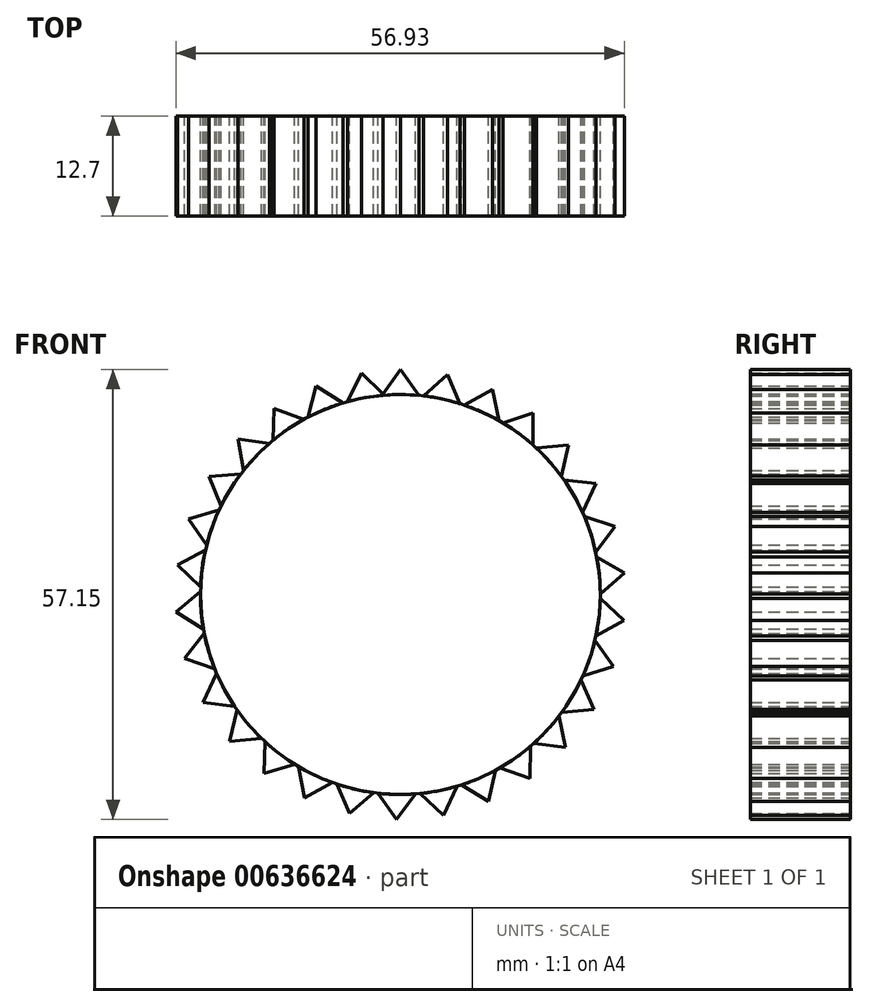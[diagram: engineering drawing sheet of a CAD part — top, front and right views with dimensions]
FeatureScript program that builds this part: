
annotation { "Feature Type Name" : "Feature", "Feature Type Description" : "" }
export const myFeature = defineFeature(function(context is Context, id is Id, definition is map)
    precondition{}
    {
        {
            var Q0;
            Q0=qCreatedBy(makeId("Front.planeOp"),FACE);
            var sketch = newSketch(context, id + "F0", { "sketchPlane" : qUnion([Q0])});
            skCircle(sketch, "E0", {"center": v(0, 0) * mm, "radius": 25.4 * mm});
            skLineSegment(sketch, "E1", {"start": v(0, 25.4) * mm, "end": v(0, 28.58) * mm});
            skLineSegment(sketch, "E2", {"start": v(0, 28.58) * mm, "end": v(-2.37, 25.29) * mm});
            skLineSegment(sketch, "E3.MirrorCS", {"start": v(0, 28.58) * mm, "end": v(2.37, 25.29) * mm});
            skLineSegment(sketch, "E4.1.0", {"start": v(5.97, 27.94) * mm, "end": v(2.97, 25.23) * mm});
            skLineSegment(sketch, "E4.1.1", {"start": v(5.97, 27.94) * mm, "end": v(7.6, 24.23) * mm});
            skLineSegment(sketch, "E4.2.0", {"start": v(11.69, 26.08) * mm, "end": v(8.17, 24.05) * mm});
            skLineSegment(sketch, "E4.2.1", {"start": v(11.69, 26.08) * mm, "end": v(12.5, 22.1) * mm});
            skLineSegment(sketch, "E4.3.0", {"start": v(16.88, 23.06) * mm, "end": v(13.02, 21.8) * mm});
            skLineSegment(sketch, "E4.3.1", {"start": v(16.88, 23.06) * mm, "end": v(16.85, 19) * mm});
            skLineSegment(sketch, "E4.4.0", {"start": v(21.33, 19.02) * mm, "end": v(17.3, 18.6) * mm});
            skLineSegment(sketch, "E4.4.1", {"start": v(21.33, 19.02) * mm, "end": v(20.45, 15.06) * mm});
            skLineSegment(sketch, "E4.5.0", {"start": v(24.83, 14.14) * mm, "end": v(20.8, 14.58) * mm});
            skLineSegment(sketch, "E4.5.1", {"start": v(24.83, 14.14) * mm, "end": v(23.15, 10.45) * mm});
            skLineSegment(sketch, "E4.6.0", {"start": v(27.24, 8.63) * mm, "end": v(23.39, 9.9) * mm});
            skLineSegment(sketch, "E4.6.1", {"start": v(27.24, 8.63) * mm, "end": v(24.82, 5.38) * mm});
            skLineSegment(sketch, "E4.7.0", {"start": v(28.44, 2.75) * mm, "end": v(24.94, 4.8) * mm});
            skLineSegment(sketch, "E4.7.1", {"start": v(28.44, 2.75) * mm, "end": v(25.4, 0.07) * mm});
            skLineSegment(sketch, "E4.8.0", {"start": v(28.39, -3.26) * mm, "end": v(25.4, -0.53) * mm});
            skLineSegment(sketch, "E4.8.1", {"start": v(28.39, -3.26) * mm, "end": v(24.85, -5.24) * mm});
            skLineSegment(sketch, "E4.9.0", {"start": v(27.08, -9.12) * mm, "end": v(24.72, -5.82) * mm});
            skLineSegment(sketch, "E4.9.1", {"start": v(27.08, -9.12) * mm, "end": v(23.2, -10.32) * mm});
            skLineSegment(sketch, "E4.10.0", {"start": v(24.57, -14.58) * mm, "end": v(22.96, -10.87) * mm});
            skLineSegment(sketch, "E4.10.1", {"start": v(24.57, -14.58) * mm, "end": v(20.54, -14.95) * mm});
            skLineSegment(sketch, "E4.11.0", {"start": v(20.98, -19.4) * mm, "end": v(20.18, -15.43) * mm});
            skLineSegment(sketch, "E4.11.1", {"start": v(20.98, -19.4) * mm, "end": v(16.96, -18.91) * mm});
            skLineSegment(sketch, "E4.12.0", {"start": v(16.46, -23.36) * mm, "end": v(16.5, -19.3) * mm});
            skLineSegment(sketch, "E4.12.1", {"start": v(16.46, -23.36) * mm, "end": v(12.63, -22.04) * mm});
            skLineSegment(sketch, "E4.13.0", {"start": v(11.21, -26.28) * mm, "end": v(12.1, -22.33) * mm});
            skLineSegment(sketch, "E4.13.1", {"start": v(11.21, -26.28) * mm, "end": v(7.74, -24.2) * mm});
            skLineSegment(sketch, "E4.14.0", {"start": v(5.47, -28.05) * mm, "end": v(7.17, -24.37) * mm});
            skLineSegment(sketch, "E4.14.1", {"start": v(5.47, -28.05) * mm, "end": v(2.5, -25.28) * mm});
            skLineSegment(sketch, "E4.15.0", {"start": v(-0.52, -28.57) * mm, "end": v(1.92, -25.33) * mm});
            skLineSegment(sketch, "E4.15.1", {"start": v(-0.52, -28.57) * mm, "end": v(-2.83, -25.24) * mm});
            skLineSegment(sketch, "E4.16.0", {"start": v(-6.48, -27.83) * mm, "end": v(-3.42, -25.17) * mm});
            skLineSegment(sketch, "E4.16.1", {"start": v(-6.48, -27.83) * mm, "end": v(-8.05, -24.1) * mm});
            skLineSegment(sketch, "E4.17.0", {"start": v(-12.15, -25.86) * mm, "end": v(-8.6, -23.9) * mm});
            skLineSegment(sketch, "E4.17.1", {"start": v(-12.15, -25.86) * mm, "end": v(-12.9, -21.88) * mm});
            skLineSegment(sketch, "E4.18.0", {"start": v(-17.3, -22.75) * mm, "end": v(-13.41, -21.57) * mm});
            skLineSegment(sketch, "E4.18.1", {"start": v(-17.3, -22.75) * mm, "end": v(-17.2, -18.7) * mm});
            skLineSegment(sketch, "E4.19.0", {"start": v(-21.67, -18.63) * mm, "end": v(-17.63, -18.29) * mm});
            skLineSegment(sketch, "E4.19.1", {"start": v(-21.67, -18.63) * mm, "end": v(-20.72, -14.69) * mm});
            skLineSegment(sketch, "E4.20.0", {"start": v(-25.08, -13.69) * mm, "end": v(-21.06, -14.2) * mm});
            skLineSegment(sketch, "E4.20.1", {"start": v(-25.08, -13.69) * mm, "end": v(-23.34, -10.03) * mm});
            skLineSegment(sketch, "E4.21.0", {"start": v(-27.4, -8.14) * mm, "end": v(-23.56, -9.48) * mm});
            skLineSegment(sketch, "E4.21.1", {"start": v(-27.4, -8.14) * mm, "end": v(-24.92, -4.93) * mm});
            skLineSegment(sketch, "E4.22.0", {"start": v(-28.49, -2.23) * mm, "end": v(-25.03, -4.34) * mm});
            skLineSegment(sketch, "E4.22.1", {"start": v(-28.49, -2.23) * mm, "end": v(-25.4, 0.4) * mm});
            skLineSegment(sketch, "E4.23.0", {"start": v(-28.32, 3.77) * mm, "end": v(-25.38, 0.98) * mm});
            skLineSegment(sketch, "E4.23.1", {"start": v(-28.32, 3.77) * mm, "end": v(-24.75, 5.7) * mm});
            skLineSegment(sketch, "E4.24.0", {"start": v(-26.91, 9.61) * mm, "end": v(-24.61, 6.27) * mm});
            skLineSegment(sketch, "E4.24.1", {"start": v(-26.91, 9.61) * mm, "end": v(-23.02, 10.74) * mm});
            skLineSegment(sketch, "E4.25.0", {"start": v(-24.3, 15.03) * mm, "end": v(-22.76, 11.28) * mm});
            skLineSegment(sketch, "E4.25.1", {"start": v(-24.3, 15.03) * mm, "end": v(-20.26, 15.32) * mm});
            skLineSegment(sketch, "E4.26.0", {"start": v(-20.63, 19.78) * mm, "end": v(-19.9, 15.79) * mm});
            skLineSegment(sketch, "E4.26.1", {"start": v(-20.63, 19.78) * mm, "end": v(-16.61, 19.22) * mm});
            skLineSegment(sketch, "E4.27.0", {"start": v(-16.04, 23.65) * mm, "end": v(-16.16, 19.6) * mm});
            skLineSegment(sketch, "E4.27.1", {"start": v(-16.04, 23.65) * mm, "end": v(-12.23, 22.26) * mm});
            skLineSegment(sketch, "E4.28.0", {"start": v(-10.74, 26.48) * mm, "end": v(-11.7, 22.54) * mm});
            skLineSegment(sketch, "E4.28.1", {"start": v(-10.74, 26.48) * mm, "end": v(-7.3, 24.33) * mm});
            skLineSegment(sketch, "E4.29.0", {"start": v(-4.96, 28.14) * mm, "end": v(-6.73, 24.5) * mm});
            skLineSegment(sketch, "E4.29.1", {"start": v(-4.96, 28.14) * mm, "end": v(-2.05, 25.32) * mm});
            skLineSegment(sketch, "E4.anchor1", {"start": v(0, 0) * mm, "end": v(-2.37, 25.29) * mm, "construction": true});
            skLineSegment(sketch, "E4.anchor2", {"start": v(0, 0) * mm, "end": v(-6.73, 24.5) * mm, "construction": true});
            skSolve(sketch);
        }
        {
            var Q0;
            {var subQ0=sQuery(id+"F0.wireOp",EDGE,"E4.1.0");Q0=makeQuery(id+"F0.imprint","IMPRINT",FACE,{"disambiguationData":[TD([[makeQuery(id+"F0.imprint","IMPRINT",EDGE,{"derivedFrom":subQ0}),1.0]])]});}
            var Q1;
            {var subQ0=sQuery(id+"F0.wireOp",EDGE,"E4.2.0");Q1=makeQuery(id+"F0.imprint","IMPRINT",FACE,{"disambiguationData":[TD([[makeQuery(id+"F0.imprint","IMPRINT",EDGE,{"derivedFrom":subQ0}),1.0]])]});}
            var Q2;
            {var subQ0=sQuery(id+"F0.wireOp",EDGE,"E4.3.0");Q2=makeQuery(id+"F0.imprint","IMPRINT",FACE,{"disambiguationData":[TD([[makeQuery(id+"F0.imprint","IMPRINT",EDGE,{"derivedFrom":subQ0}),1.0]])]});}
            var Q3;
            {var subQ0=sQuery(id+"F0.wireOp",EDGE,"E4.4.0");Q3=makeQuery(id+"F0.imprint","IMPRINT",FACE,{"disambiguationData":[TD([[makeQuery(id+"F0.imprint","IMPRINT",EDGE,{"derivedFrom":subQ0}),1.0]])]});}
            var Q4;
            {var subQ0=sQuery(id+"F0.wireOp",EDGE,"E4.5.0");Q4=makeQuery(id+"F0.imprint","IMPRINT",FACE,{"disambiguationData":[TD([[makeQuery(id+"F0.imprint","IMPRINT",EDGE,{"derivedFrom":subQ0}),1.0]])]});}
            var Q5;
            {var subQ0=sQuery(id+"F0.wireOp",EDGE,"E4.6.0");Q5=makeQuery(id+"F0.imprint","IMPRINT",FACE,{"disambiguationData":[TD([[makeQuery(id+"F0.imprint","IMPRINT",EDGE,{"derivedFrom":subQ0}),1.0]])]});}
            var Q6;
            {var subQ0=sQuery(id+"F0.wireOp",EDGE,"E4.7.0");Q6=makeQuery(id+"F0.imprint","IMPRINT",FACE,{"disambiguationData":[TD([[makeQuery(id+"F0.imprint","IMPRINT",EDGE,{"derivedFrom":subQ0}),1.0]])]});}
            var Q7;
            {var subQ0=sQuery(id+"F0.wireOp",EDGE,"E4.8.0");Q7=makeQuery(id+"F0.imprint","IMPRINT",FACE,{"disambiguationData":[TD([[makeQuery(id+"F0.imprint","IMPRINT",EDGE,{"derivedFrom":subQ0}),1.0]])]});}
            var Q8;
            {var subQ0=sQuery(id+"F0.wireOp",EDGE,"E4.9.0");Q8=makeQuery(id+"F0.imprint","IMPRINT",FACE,{"disambiguationData":[TD([[makeQuery(id+"F0.imprint","IMPRINT",EDGE,{"derivedFrom":subQ0}),1.0]])]});}
            var Q9;
            {var subQ0=sQuery(id+"F0.wireOp",EDGE,"E4.10.0");Q9=makeQuery(id+"F0.imprint","IMPRINT",FACE,{"disambiguationData":[TD([[makeQuery(id+"F0.imprint","IMPRINT",EDGE,{"derivedFrom":subQ0}),1.0]])]});}
            var Q10;
            {var subQ0=sQuery(id+"F0.wireOp",EDGE,"E4.11.0");Q10=makeQuery(id+"F0.imprint","IMPRINT",FACE,{"disambiguationData":[TD([[makeQuery(id+"F0.imprint","IMPRINT",EDGE,{"derivedFrom":subQ0}),1.0]])]});}
            var Q11;
            {var subQ0=sQuery(id+"F0.wireOp",EDGE,"E4.12.0");Q11=makeQuery(id+"F0.imprint","IMPRINT",FACE,{"disambiguationData":[TD([[makeQuery(id+"F0.imprint","IMPRINT",EDGE,{"derivedFrom":subQ0}),1.0]])]});}
            var Q12;
            {var subQ0=sQuery(id+"F0.wireOp",EDGE,"E4.13.0");Q12=makeQuery(id+"F0.imprint","IMPRINT",FACE,{"disambiguationData":[TD([[makeQuery(id+"F0.imprint","IMPRINT",EDGE,{"derivedFrom":subQ0}),1.0]])]});}
            var Q13;
            {var subQ0=sQuery(id+"F0.wireOp",EDGE,"E4.14.0");Q13=makeQuery(id+"F0.imprint","IMPRINT",FACE,{"disambiguationData":[TD([[makeQuery(id+"F0.imprint","IMPRINT",EDGE,{"derivedFrom":subQ0}),1.0]])]});}
            var Q14;
            {var subQ0=sQuery(id+"F0.wireOp",EDGE,"E4.15.0");Q14=makeQuery(id+"F0.imprint","IMPRINT",FACE,{"disambiguationData":[TD([[makeQuery(id+"F0.imprint","IMPRINT",EDGE,{"derivedFrom":subQ0}),1.0]])]});}
            var Q15;
            {var subQ0=sQuery(id+"F0.wireOp",EDGE,"E4.16.0");Q15=makeQuery(id+"F0.imprint","IMPRINT",FACE,{"disambiguationData":[TD([[makeQuery(id+"F0.imprint","IMPRINT",EDGE,{"derivedFrom":subQ0}),1.0]])]});}
            var Q16;
            {var subQ0=sQuery(id+"F0.wireOp",EDGE,"E4.17.0");Q16=makeQuery(id+"F0.imprint","IMPRINT",FACE,{"disambiguationData":[TD([[makeQuery(id+"F0.imprint","IMPRINT",EDGE,{"derivedFrom":subQ0}),1.0]])]});}
            var Q17;
            {var subQ0=sQuery(id+"F0.wireOp",EDGE,"E4.18.0");Q17=makeQuery(id+"F0.imprint","IMPRINT",FACE,{"disambiguationData":[TD([[makeQuery(id+"F0.imprint","IMPRINT",EDGE,{"derivedFrom":subQ0}),1.0]])]});}
            var Q18;
            {var subQ0=sQuery(id+"F0.wireOp",EDGE,"E4.19.0");Q18=makeQuery(id+"F0.imprint","IMPRINT",FACE,{"disambiguationData":[TD([[makeQuery(id+"F0.imprint","IMPRINT",EDGE,{"derivedFrom":subQ0}),1.0]])]});}
            var Q19;
            {var subQ0=sQuery(id+"F0.wireOp",EDGE,"E4.20.0");Q19=makeQuery(id+"F0.imprint","IMPRINT",FACE,{"disambiguationData":[TD([[makeQuery(id+"F0.imprint","IMPRINT",EDGE,{"derivedFrom":subQ0}),1.0]])]});}
            var Q20;
            {var subQ0=sQuery(id+"F0.wireOp",EDGE,"E4.21.0");Q20=makeQuery(id+"F0.imprint","IMPRINT",FACE,{"disambiguationData":[TD([[makeQuery(id+"F0.imprint","IMPRINT",EDGE,{"derivedFrom":subQ0}),1.0]])]});}
            var Q21;
            {var subQ0=sQuery(id+"F0.wireOp",EDGE,"E4.22.0");Q21=makeQuery(id+"F0.imprint","IMPRINT",FACE,{"disambiguationData":[TD([[makeQuery(id+"F0.imprint","IMPRINT",EDGE,{"derivedFrom":subQ0}),1.0]])]});}
            var Q22;
            {var subQ0=sQuery(id+"F0.wireOp",EDGE,"E4.23.0");Q22=makeQuery(id+"F0.imprint","IMPRINT",FACE,{"disambiguationData":[TD([[makeQuery(id+"F0.imprint","IMPRINT",EDGE,{"derivedFrom":subQ0}),1.0]])]});}
            var Q23;
            {var subQ0=sQuery(id+"F0.wireOp",EDGE,"E4.24.0");Q23=makeQuery(id+"F0.imprint","IMPRINT",FACE,{"disambiguationData":[TD([[makeQuery(id+"F0.imprint","IMPRINT",EDGE,{"derivedFrom":subQ0}),1.0]])]});}
            var Q24;
            {var subQ0=sQuery(id+"F0.wireOp",EDGE,"E4.25.0");Q24=makeQuery(id+"F0.imprint","IMPRINT",FACE,{"disambiguationData":[TD([[makeQuery(id+"F0.imprint","IMPRINT",EDGE,{"derivedFrom":subQ0}),1.0]])]});}
            var Q25;
            {var subQ0=sQuery(id+"F0.wireOp",EDGE,"E4.26.0");Q25=makeQuery(id+"F0.imprint","IMPRINT",FACE,{"disambiguationData":[TD([[makeQuery(id+"F0.imprint","IMPRINT",EDGE,{"derivedFrom":subQ0}),1.0]])]});}
            var Q26;
            {var subQ0=sQuery(id+"F0.wireOp",EDGE,"E4.27.0");Q26=makeQuery(id+"F0.imprint","IMPRINT",FACE,{"disambiguationData":[TD([[makeQuery(id+"F0.imprint","IMPRINT",EDGE,{"derivedFrom":subQ0}),1.0]])]});}
            var Q27;
            {var subQ0=sQuery(id+"F0.wireOp",EDGE,"E4.28.0");Q27=makeQuery(id+"F0.imprint","IMPRINT",FACE,{"disambiguationData":[TD([[makeQuery(id+"F0.imprint","IMPRINT",EDGE,{"derivedFrom":subQ0}),1.0]])]});}
            var Q28;
            {var subQ0=sQuery(id+"F0.wireOp",EDGE,"E1");Q28=makeQuery(id+"F0.imprint","IMPRINT",FACE,{"disambiguationData":[TD([[makeQuery(id+"F0.imprint","IMPRINT",EDGE,{"derivedFrom":subQ0}),-1.0]])]});}
            var Q29;
            {var subQ5=sQuery(id+"F0.wireOp",EDGE,"E4.29.0");Q29=makeQuery(id+"F0.imprint","IMPRINT",FACE,{"disambiguationData":[TD([[makeQuery(id+"F0.imprint","IMPRINT",EDGE,{"derivedFrom":subQ5}),1.0]])]});}
            var Q30;
            {var subQ0=sQuery(id+"F0.wireOp",EDGE,"E1");Q30=makeQuery(id+"F0.imprint","IMPRINT",FACE,{"disambiguationData":[TD([[makeQuery(id+"F0.imprint","IMPRINT",EDGE,{"derivedFrom":subQ0}),1.0]])]});}
            var Q31;
            {var subQ0=sQuery(id+"F0.wireOp",EDGE,"E0");var subQ1=sQuery(id+"F0.wireOp",EDGE,"E2");var subQ2=makeQuery(id+"F0.imprint","INTERSECT",VERTEX,{"derivedFrom":[subQ1,subQ0]});Q31=makeQuery(id+"F0.imprint","IMPRINT",FACE,{"disambiguationData":[TD([[makeQuery(id+"F0.imprint","IMPRINT",EDGE,{"disambiguationData":[TD([[subQ2,1.0]])],"derivedFrom":subQ1}),1.0]])]});}
            extrude(context, id + "F1", {"entities" : qUnion([Q0, Q1, Q2, Q3, Q4, Q5, Q6, Q7, Q8, Q9, Q10, Q11, Q12, Q13, Q14, Q15, Q16, Q17, Q18, Q19, Q20, Q21, Q22, Q23, Q24, Q25, Q26, Q27, Q28, Q29, Q30, Q31]), "depth" : 12.7 * mm, "offsetDistance" : 25.4 * mm});
        }
        {
            var Q0;
            {var subQ0=sQuery(id+"F0.wireOp",EDGE,"E0");var subQ33=makeQuery(id+"F0.imprint","INTERSECT",VERTEX,{"derivedFrom":[sQuery(id+"F0.wireOp",EDGE,"E4.6.1"),subQ0]});Q0=makeQuery(id+"F0.imprint","IMPRINT",FACE,{"disambiguationData":[TD([[makeQuery(id+"F0.imprint","IMPRINT",EDGE,{"disambiguationData":[TD([[subQ33,1.0]])],"derivedFrom":subQ0}),1.0]])]});}
            extrude(context, id + "F2", {"entities" : qUnion([Q0]), "depth" : 12.7 * mm, "offsetDistance" : 25.4 * mm});
        }
    });
